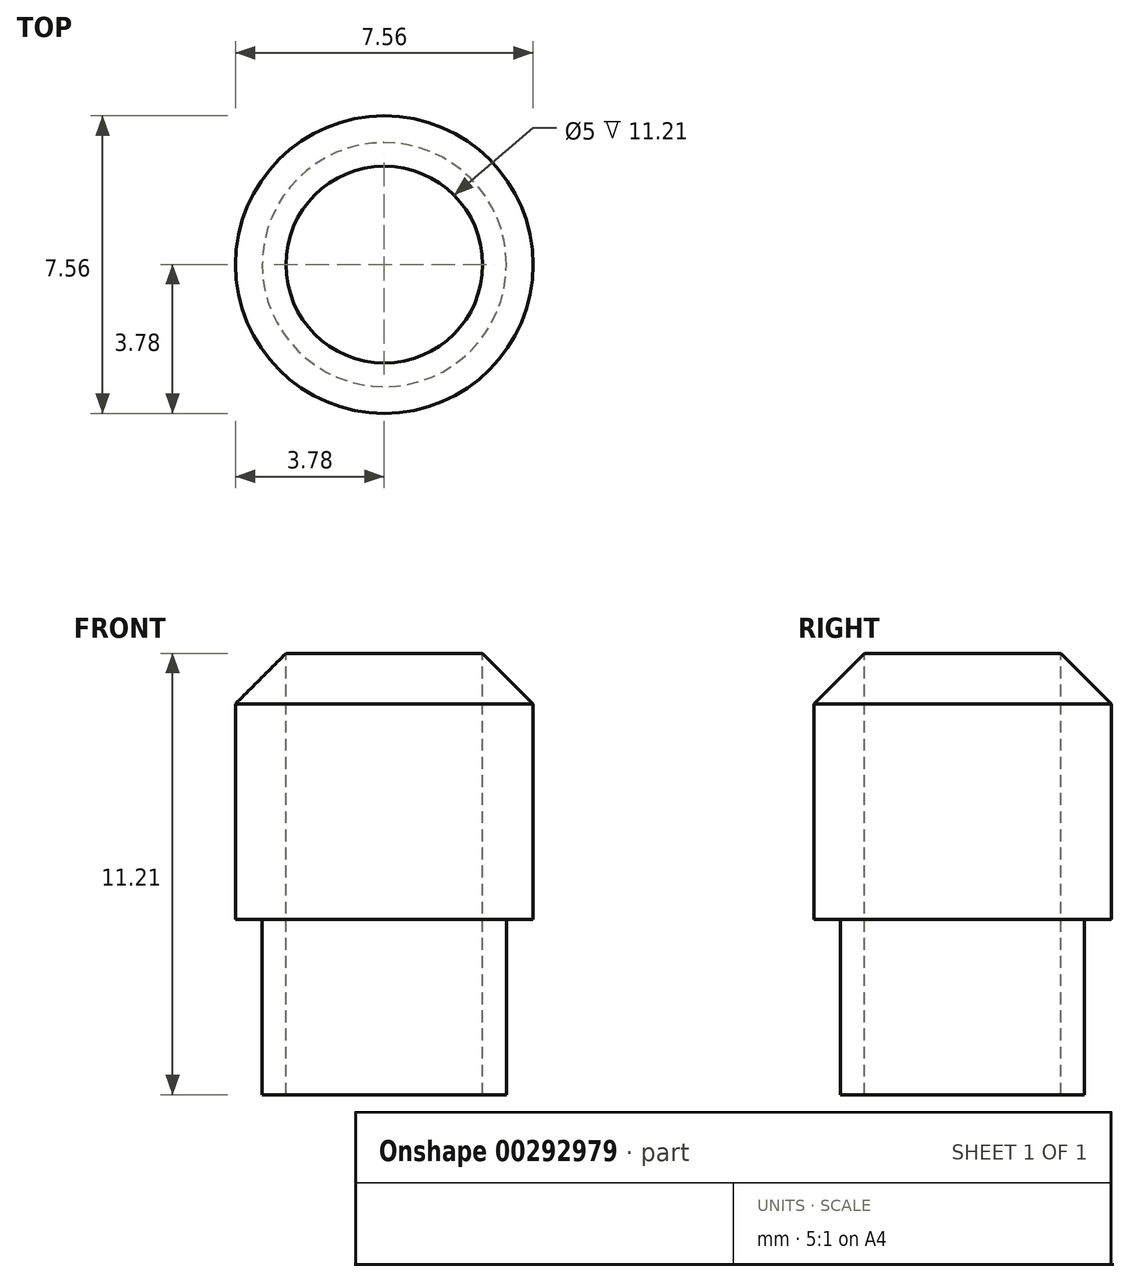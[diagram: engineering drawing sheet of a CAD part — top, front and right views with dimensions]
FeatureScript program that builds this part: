
annotation { "Feature Type Name" : "Feature", "Feature Type Description" : "" }
export const myFeature = defineFeature(function(context is Context, id is Id, definition is map)
    precondition{}
    {
        {
            var Q0;
            Q0=qCreatedBy(makeId("Top.planeOp"),FACE);
            var sketch = newSketch(context, id + "F0", { "sketchPlane" : qUnion([Q0])});
            skCircle(sketch, "E0", {"center": v(0, 0) * mm, "radius": 3.78 * mm});
            skSolve(sketch);
        }
        {
            var Q0;
            Q0 = qSketchRegion(id + "F0", true);
            extrude(context, id + "F1", {"entities" : qUnion([Q0]), "depth" : 6.88 * mm});
        }
        {
            var Q0;
            Q0=makeQuery(id+"F1.opExtrude","CAP_FACE",FACE,{"disambiguationData":[OSD([sQuery(id+"F0.wireOp",EDGE,"E0")])],"isStart":true});
            var sketch = newSketch(context, id + "F2", { "sketchPlane" : qUnion([Q0])});
            skCircle(sketch, "E1", {"center": v(0, 0) * mm, "radius": 3.1 * mm});
            skSolve(sketch);
        }
        {
            var Q0;
            Q0=makeQuery(id+"F2.imprint","IMPRINT",FACE,{"disambiguationData":[TD([[makeQuery(id+"F2.imprint","IMPRINT",EDGE,{"derivedFrom":sQuery(id+"F2.wireOp",EDGE,"E1")}),1.0]])]});
            extrude(context, id + "F3", {"entities" : qUnion([Q0]), "operationType" : NewBodyOperationType.ADD, "depth" : 4.45 * mm});
        }
        {
            var Q0;
            Q0=makeQuery(id+"F1.opExtrude","CAP_FACE",FACE,{"disambiguationData":[OSD([sQuery(id+"F0.wireOp",EDGE,"E0")])],"isStart":false});
            var sketch = newSketch(context, id + "F4", { "sketchPlane" : qUnion([Q0])});
            skCircle(sketch, "E2", {"center": v(0, 0) * mm, "radius": 2.5 * mm});
            skSolve(sketch);
        }
        {
            var Q0;
            Q0=makeQuery(id+"F4.imprint","IMPRINT",FACE,{"disambiguationData":[TD([[makeQuery(id+"F4.imprint","IMPRINT",EDGE,{"derivedFrom":sQuery(id+"F4.wireOp",EDGE,"E2")}),1.0]])]});
            extrude(context, id + "F5", {"entities" : qUnion([Q0]), "operationType" : NewBodyOperationType.REMOVE, "oppositeDirection" : true, "depth" : 11.6 * mm});
        }
        {
            var Q0;
            Q0=makeQuery(id+"F1.opExtrude","CAP_EDGE",EDGE,{"disambiguationData":[OSD([sQuery(id+"F0.wireOp",EDGE,"E0")])],"isStart":false});
            chamfer(context, id + "F6", {"entities" : qUnion([Q0]), "width" : 1.4 * mm, "tangentPropagation" : true});
        }
    });
